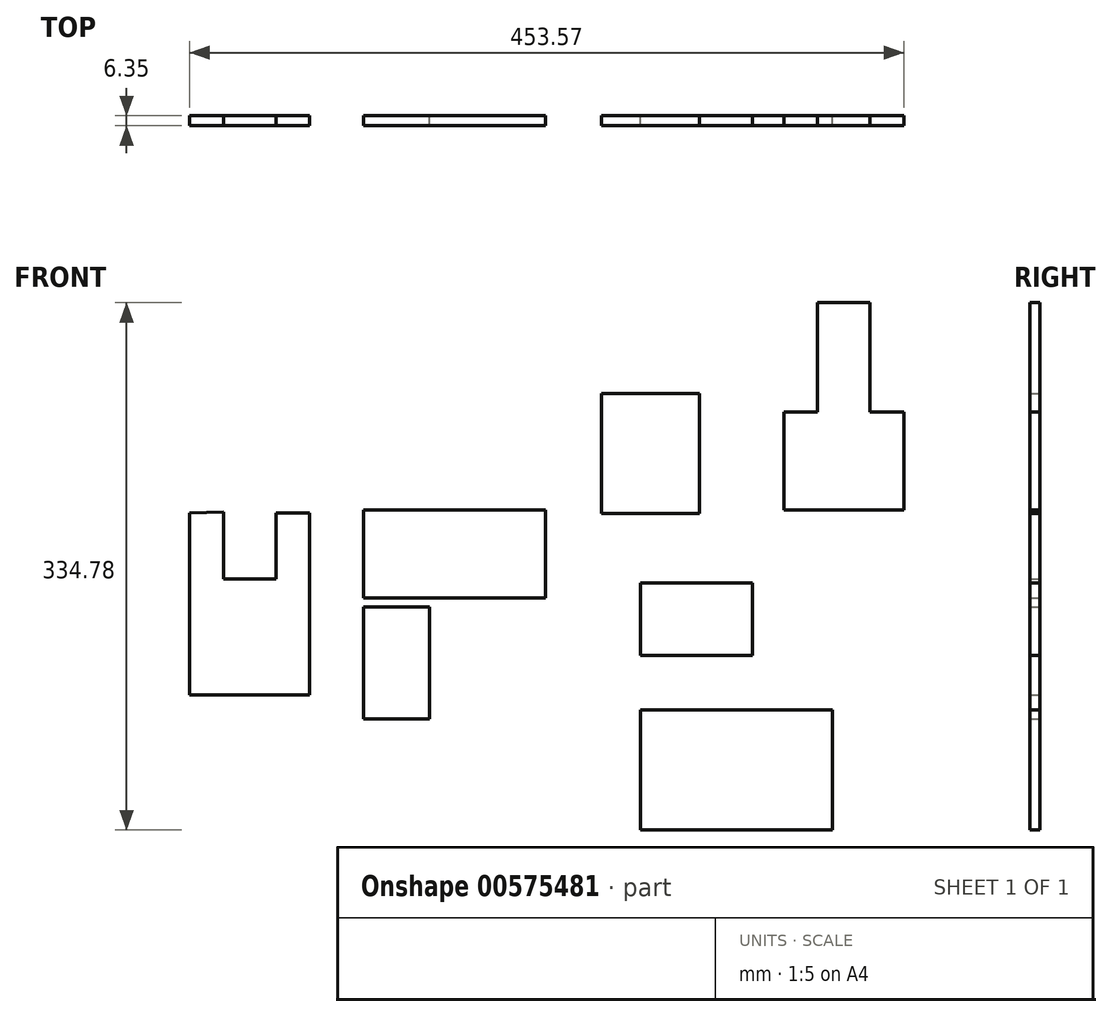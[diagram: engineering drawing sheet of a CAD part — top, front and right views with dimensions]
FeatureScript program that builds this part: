
annotation { "Feature Type Name" : "Feature", "Feature Type Description" : "" }
export const myFeature = defineFeature(function(context is Context, id is Id, definition is map)
    precondition{}
    {
        {
            var Q0;
            Q0=qCreatedBy(makeId("Front.planeOp"),FACE);
            var sketch = newSketch(context, id + "F0", { "sketchPlane" : qUnion([Q0])});
            skLineSegment(sketch, "E0", {"start": v(67.58, 0) * mm, "end": v(-48.1, 0) * mm});
            skLineSegment(sketch, "E1", {"start": v(103.02, 73.87) * mm, "end": v(103.02, -2.33) * mm});
            skLineSegment(sketch, "E2", {"start": v(127.76, -46.31) * mm, "end": v(127.76, -92.31) * mm});
            skLineSegment(sketch, "E3", {"start": v(67.58, 0) * mm, "end": v(67.58, -55.88) * mm});
            skLineSegment(sketch, "E4", {"start": v(67.58, -55.88) * mm, "end": v(-6.08, -55.88) * mm});
            skLineSegment(sketch, "E5", {"start": v(-48.1, 0) * mm, "end": v(-48.1, -55.88) * mm});
            skLineSegment(sketch, "E6", {"start": v(-48.1, -61.58) * mm, "end": v(-48.1, -132.7) * mm});
            skLineSegment(sketch, "E7", {"start": v(-6.08, -61.58) * mm, "end": v(-6.08, -132.7) * mm});
            skLineSegment(sketch, "E8", {"start": v(-6.08, -132.7) * mm, "end": v(-48.1, -132.7) * mm});
            skLineSegment(sketch, "E9", {"start": v(127.76, -92.31) * mm, "end": v(198.88, -92.31) * mm});
            skLineSegment(sketch, "E10", {"start": v(198.88, -92.31) * mm, "end": v(198.88, -46.31) * mm});
            skLineSegment(sketch, "E11", {"start": v(198.88, -46.31) * mm, "end": v(127.76, -46.31) * mm});
            skLineSegment(sketch, "E12", {"start": v(127.76, -127.03) * mm, "end": v(127.76, -203.23) * mm});
            skLineSegment(sketch, "E13", {"start": v(127.76, -203.23) * mm, "end": v(249.78, -203.23) * mm});
            skLineSegment(sketch, "E14", {"start": v(249.78, -203.23) * mm, "end": v(249.78, -127.03) * mm});
            skLineSegment(sketch, "E15", {"start": v(249.78, -127.03) * mm, "end": v(127.76, -127.03) * mm});
            skLineSegment(sketch, "E16", {"start": v(103.02, 73.87) * mm, "end": v(165.25, 73.87) * mm});
            skLineSegment(sketch, "E17", {"start": v(165.25, 73.87) * mm, "end": v(165.25, -2.33) * mm});
            skLineSegment(sketch, "E18", {"start": v(165.25, -2.33) * mm, "end": v(103.02, -2.33) * mm});
            skLineSegment(sketch, "E19", {"start": v(-6.08, -61.58) * mm, "end": v(-48.1, -61.58) * mm});
            skLineSegment(sketch, "E20", {"start": v(-48.1, -55.88) * mm, "end": v(-6.08, -55.88) * mm});
            skLineSegment(sketch, "E21", {"start": v(-158.43, -1.92) * mm, "end": v(-158.43, -117.6) * mm});
            skLineSegment(sketch, "E22", {"start": v(-158.43, -117.6) * mm, "end": v(-82.23, -117.6) * mm});
            skLineSegment(sketch, "E23", {"start": v(-82.23, -117.6) * mm, "end": v(-82.23, -1.92) * mm});
            skLineSegment(sketch, "E24", {"start": v(-82.23, -1.92) * mm, "end": v(-103.68, -1.92) * mm});
            skLineSegment(sketch, "E25", {"start": v(-103.68, -1.92) * mm, "end": v(-103.68, -43.93) * mm});
            skLineSegment(sketch, "E26", {"start": v(-103.68, -43.93) * mm, "end": v(-136.98, -43.93) * mm});
            skLineSegment(sketch, "E27", {"start": v(-136.98, -43.93) * mm, "end": v(-136.99, -1.3) * mm});
            skLineSegment(sketch, "E28", {"start": v(-136.99, -1.3) * mm, "end": v(-158.43, -1.92) * mm});
            skLineSegment(sketch, "E29", {"start": v(218.94, 62.23) * mm, "end": v(218.94, 0) * mm});
            skLineSegment(sketch, "E30", {"start": v(218.94, 0) * mm, "end": v(295.14, 0) * mm});
            skLineSegment(sketch, "E31", {"start": v(295.14, 0) * mm, "end": v(295.14, 62.23) * mm});
            skLineSegment(sketch, "E32", {"start": v(273.7, 131.55) * mm, "end": v(240.4, 131.55) * mm});
            skLineSegment(sketch, "E33", {"start": v(218.94, 62.23) * mm, "end": v(240.4, 62.23) * mm});
            skLineSegment(sketch, "E34.trimOffspring", {"start": v(273.7, 62.23) * mm, "end": v(295.14, 62.23) * mm});
            skLineSegment(sketch, "E35", {"start": v(240.4, 62.23) * mm, "end": v(240.4, 131.55) * mm});
            skLineSegment(sketch, "E36", {"start": v(273.7, 62.23) * mm, "end": v(273.7, 131.55) * mm});
            skSolve(sketch);
        }
        {
            var Q0;
            Q0=makeQuery(id+"F0.imprint","IMPRINT",FACE,{"disambiguationData":[TD([[makeQuery(id+"F0.imprint","IMPRINT",EDGE,{"derivedFrom":sQuery(id+"F0.wireOp",EDGE,"E21")}),1.0]])]});
            var Q1;
            Q1=makeQuery(id+"F0.imprint","IMPRINT",FACE,{"disambiguationData":[TD([[makeQuery(id+"F0.imprint","IMPRINT",EDGE,{"derivedFrom":sQuery(id+"F0.wireOp",EDGE,"E6")}),1.0]])]});
            var Q2;
            Q2=makeQuery(id+"F0.imprint","IMPRINT",FACE,{"disambiguationData":[TD([[makeQuery(id+"F0.imprint","IMPRINT",EDGE,{"derivedFrom":sQuery(id+"F0.wireOp",EDGE,"E0")}),1.0]])]});
            var Q3;
            Q3=makeQuery(id+"F0.imprint","IMPRINT",FACE,{"disambiguationData":[TD([[makeQuery(id+"F0.imprint","IMPRINT",EDGE,{"derivedFrom":sQuery(id+"F0.wireOp",EDGE,"E1")}),1.0]])]});
            var Q4;
            Q4=makeQuery(id+"F0.imprint","IMPRINT",FACE,{"disambiguationData":[TD([[makeQuery(id+"F0.imprint","IMPRINT",EDGE,{"derivedFrom":sQuery(id+"F0.wireOp",EDGE,"E29")}),1.0]])]});
            var Q5;
            Q5=makeQuery(id+"F0.imprint","IMPRINT",FACE,{"disambiguationData":[TD([[makeQuery(id+"F0.imprint","IMPRINT",EDGE,{"derivedFrom":sQuery(id+"F0.wireOp",EDGE,"E2")}),1.0]])]});
            var Q6;
            Q6=makeQuery(id+"F0.imprint","IMPRINT",FACE,{"disambiguationData":[TD([[makeQuery(id+"F0.imprint","IMPRINT",EDGE,{"derivedFrom":sQuery(id+"F0.wireOp",EDGE,"E12")}),1.0]])]});
            extrude(context, id + "F1", {"entities" : qUnion([Q0, Q1, Q2, Q3, Q4, Q5, Q6]), "depth" : 6.35 * mm, "offsetDistance" : 25.4 * mm});
        }
    });
